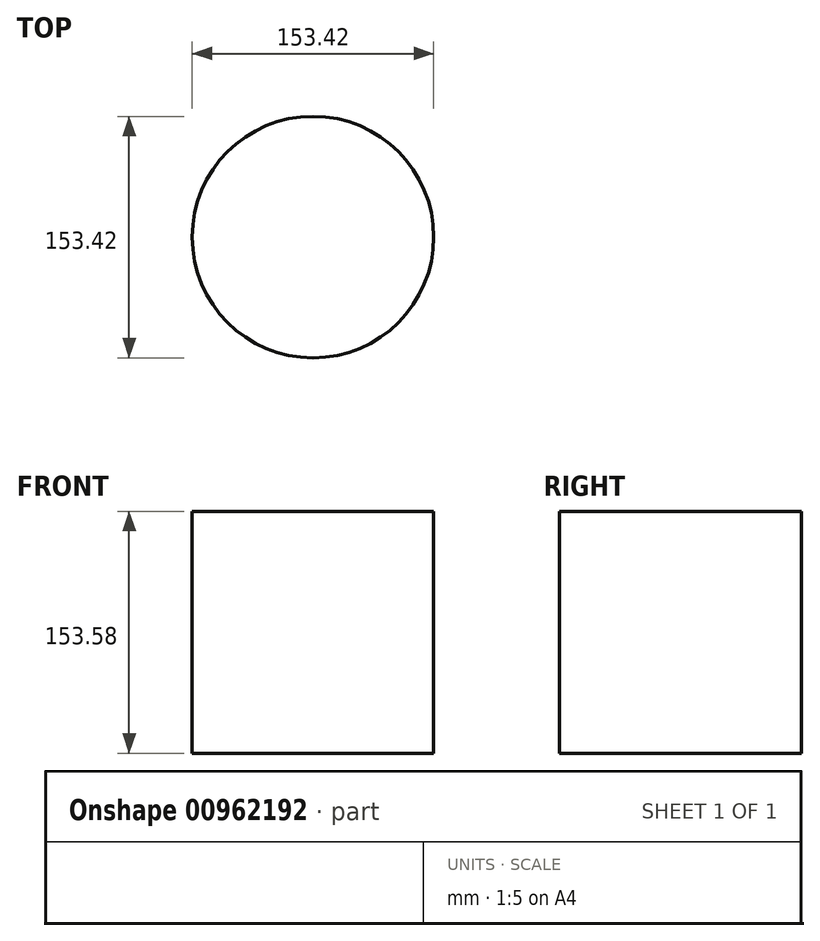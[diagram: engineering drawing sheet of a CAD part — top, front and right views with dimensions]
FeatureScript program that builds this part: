
annotation { "Feature Type Name" : "Feature", "Feature Type Description" : "" }
export const myFeature = defineFeature(function(context is Context, id is Id, definition is map)
    precondition{}
    {
        {
            var Q0;
            Q0=qCreatedBy(makeId("Top.planeOp"),FACE);
            var sketch = newSketch(context, id + "F0", { "sketchPlane" : qUnion([Q0])});
            skCircle(sketch, "E0", {"center": v(0, 0) * mm, "radius": 76.7 * mm});
            skSolve(sketch);
        }
        {
            var Q0;
            Q0 = qSketchRegion(id + "F0", true);
            extrude(context, id + "F1", {"entities" : qUnion([Q0]), "oppositeDirection" : true, "depth" : 76.99 * mm, "offsetDistance" : 25.4 * mm});
        }
        {
            var Q0;
            Q0 = qSketchRegion(id + "F0", true);
            extrude(context, id + "F2", {"entities" : qUnion([Q0]), "operationType" : NewBodyOperationType.ADD, "depth" : 76.6 * mm, "offsetDistance" : 25.4 * mm});
        }
    });
